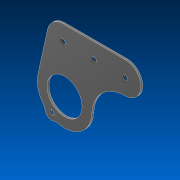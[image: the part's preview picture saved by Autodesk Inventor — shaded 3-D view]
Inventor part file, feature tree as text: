
AUTODESK INVENTOR PART (.ipt)
format: ipt  version: 2022.2 (Build 262287000, 287)  size: 128,512 bytes
history: native  units: in
note: dims shown in document units (in); Inventor stores cm internally (conversion verified against a paired STEP export)
features: extrude x1, sketch x1
ambient origin geometry x8: Origin, YZ Plane, XZ Plane, XY Plane, X Axis, Y Axis, Z Axis, Center Point
bodies: Solid1 (feature_tree)
feature tree (2):
  extrude  "Extrusion1"  Depth=2.4518in
  sketch  "Sketch1"  dims[d0=1.0in d2=2.4518in d3=1.4944in d4=0.163in d5=1.125in d6=1.75in d7=1.0in d8=0.0625in d9=0.0in d10=0.25in d11=1.3in d12=0.315in]
